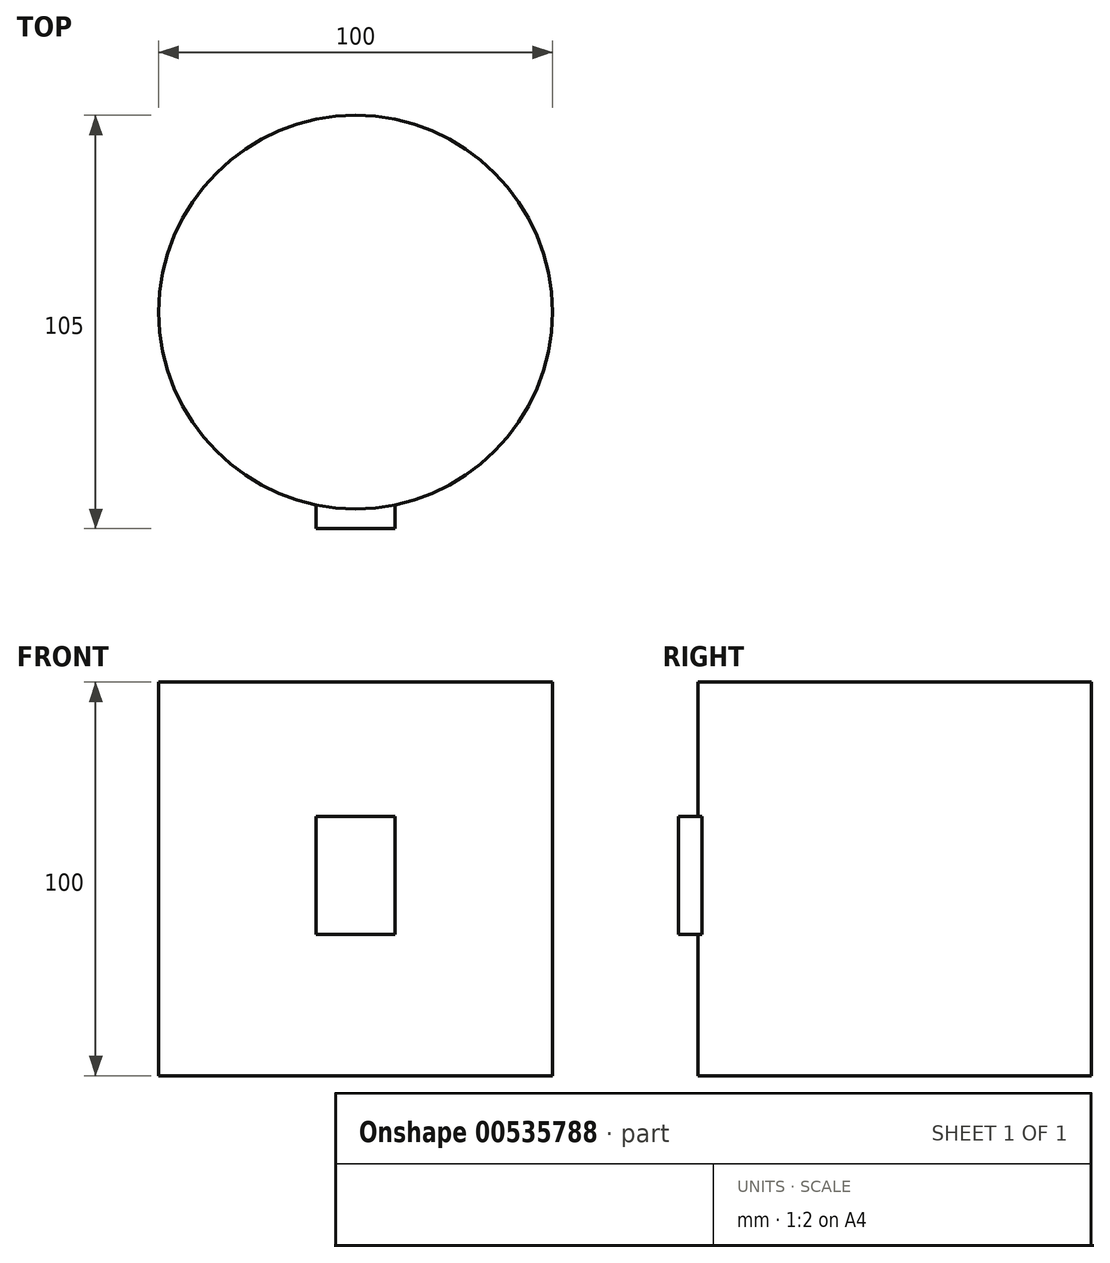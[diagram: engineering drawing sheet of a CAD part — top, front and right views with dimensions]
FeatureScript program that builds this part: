
annotation { "Feature Type Name" : "Feature", "Feature Type Description" : "" }
export const myFeature = defineFeature(function(context is Context, id is Id, definition is map)
    precondition{}
    {
        {
            var Q0;
            Q0=qCreatedBy(makeId("Top.planeOp"),FACE);
            var sketch = newSketch(context, id + "F0", { "sketchPlane" : qUnion([Q0])});
            skCircle(sketch, "E0", {"center": v(0, 0) * mm, "radius": 50 * mm});
            skSolve(sketch);
        }
        {
            var Q0;
            Q0=makeQuery(id+"F0.imprint","IMPRINT",FACE,{"disambiguationData":[TD([[makeQuery(id+"F0.imprint","IMPRINT",EDGE,{"derivedFrom":sQuery(id+"F0.wireOp",EDGE,"E0")}),1.0]])]});
            extrude(context, id + "F1", {"entities" : qUnion([Q0]), "depth" : 100 * mm, "offsetDistance" : 25 * mm});
        }
        {
            var Q0;
            Q0=qCreatedBy(makeId("Front.planeOp"),FACE);
            var sketch = newSketch(context, id + "F2", { "sketchPlane" : qUnion([Q0])});
            skLineSegment(sketch, "E1.bottom", {"start": v(-10, 35.84) * mm, "end": v(10, 35.84) * mm});
            skLineSegment(sketch, "E1.top", {"start": v(-10, 65.84) * mm, "end": v(10, 65.84) * mm});
            skLineSegment(sketch, "E1.left", {"start": v(-10, 35.84) * mm, "end": v(-10, 65.84) * mm});
            skLineSegment(sketch, "E1.right", {"start": v(10, 35.84) * mm, "end": v(10, 65.84) * mm});
            skPoint(sketch, "E1.middle", {"position": v(0, 50.84) * mm});
            skSolve(sketch);
        }
        {
            var Q0;
            Q0 = qSketchRegion(id + "F2", true);
            extrude(context, id + "F3", {"entities" : qUnion([Q0]), "operationType" : NewBodyOperationType.ADD, "depth" : 55 * mm, "offsetDistance" : 25 * mm});
        }
    });
